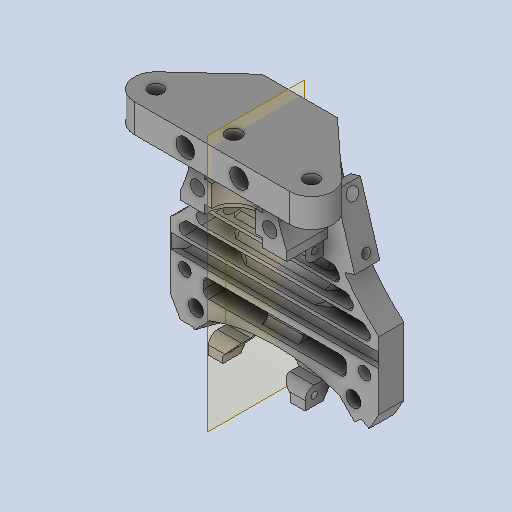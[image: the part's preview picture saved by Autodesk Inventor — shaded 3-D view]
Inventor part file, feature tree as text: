
AUTODESK INVENTOR PART (.ipt)
format: ipt  version: 2022 (Build 260153000, 153)  size: 1,126,400 bytes
history: native  units: mm
features: extrude x19, sketch x19, projected_geometry x13, reference x9, other x7, chamfer x6, fillet x4, plane x3, mirror x3, pattern_circular x1
ambient origin geometry x8: Origin, YZ Plane, XZ Plane, XY Plane, X Axis, Y Axis, Z Axis, Center Point
bodies: Solid1 (feature_tree)
feature tree (84):
  extrude  "Extrusion1"  Depth=13.0mm
  extrude  "Extrusion2"  Depth=9.0mm
  pattern_circular  "Circular Pattern1"  Count=3 Angle=360.0deg
  extrude  "Extrusion6"  Depth=7.0mm TaperAngle=0.0deg
  plane  "Work Plane1"
  extrude  "Extrusion7"  Depth=15.0mm
  extrude  "Extrusion8"  Depth=8.0mm
  extrude  "Extrusion9"  Depth=24.25mm TaperAngle=0.0deg
  fillet  "Fillet2"  Radius=30.0mm
  fillet  "Fillet3"  Radius=4.0mm
  extrude  "Extrusion10"  Depth=15.0mm
  chamfer  "Chamfer3"  Distance=3.425mm
  extrude  "Extrusion11"  TaperAngle=0.0deg  [1 undecoded]
  chamfer  "Chamfer4"  Distance=21.0mm
  extrude  "Extrusion12"  Depth=10.0mm
  extrude  "Extrusion13"  Depth=10.0mm
  extrude  "Extrusion14"  Depth=10.0mm
  extrude  "Extrusion15"  Depth=10.0mm TaperAngle=0.0deg
  extrude  "Extrusion16"  Depth=10.0mm
  mirror  "Mirror1"
  extrude  "Extrusion17"  Depth=10.0mm
  extrude  "Extrusion18"  Depth=10.0mm
  chamfer  "Chamfer5"  Distance=30.0mm
  chamfer  "Chamfer6"  Distance=30.0mm
  extrude  "Extrusion19"  Depth=10.0mm
  mirror  "Mirror2"
  plane  "Work Plane3"
  extrude  "Extrusion20"  Depth=10.0mm
  fillet  "Fillet4"  Radius=5.0mm
  mirror  "Mirror3"
  extrude  "Extrusion21"  Depth=10.0mm TaperAngle=0.0deg
  chamfer  "Chamfer7"  Distance=2.0mm
  fillet  "Fillet5"  Radius=5.0mm
  extrude  "Extrusion22"  Depth=10.0mm
  chamfer  "Chamfer8"  Distance=1.5mm
  sketch  "Sketch1"  dims[d0=25.8mm d1=13.0mm]
  sketch  "Sketch2"  dims[d2=15.0mm d3=9.0mm]
  sketch  "Sketch6"  dims[d4=8.0mm]
  sketch  "Sketch7"  dims[d5=5.0mm]
  projected_geometry  "Projected Loop1"
  projected_geometry  "Projected Loop2"
  sketch  "Sketch8"  dims[d6=25.0mm]
  sketch  "Sketch9"  dims[d7=4.0mm d8=30.0mm d10=360.0deg]
  projected_geometry  "Projected Loop3"
  projected_geometry  "Projected Loop4"
  projected_geometry  "Projected Loop5"
  projected_geometry  "Projected Loop6"
  projected_geometry  "Projected Loop7"
  sketch  "Sketch10"  dims[d12=30.0mm d14=360.0deg d16=7.0mm d17=0.0mm]
  reference  "Reference1"
  sketch  "Sketch11"  dims[d18=13.0mm d19=15.0mm]
  projected_geometry  "Projected Loop8"
  sketch  "Sketch12"  dims[d20=9.0mm d21=8.0mm]
  projected_geometry  "Projected Loop9"
  sketch  "Sketch13"  dims[d22=5.0mm d24=24.25mm d25=0.0mm d41=30.0mm d42=360.0deg d52=4.0mm]
  reference  "Reference2"
  projected_geometry  "Projected Loop10"
  sketch  "Sketch14"  dims[d53=4.0mm d54=15.0mm]
  reference  "Reference3"
  projected_geometry  "Projected Loop11"
  sketch  "Sketch15"  dims[d55=30.0mm]
  projected_geometry  "Projected Loop12"
  sketch  "Sketch16"  dims[d56=4.0mm]
  plane  "Work Plane2"
  sketch  "Sketch17"  dims[d57=4.0mm]
  sketch  "Sketch18"  dims[d58=68.718732mm]
  reference  "Reference5"
  reference  "Reference6"
  sketch  "Sketch20"  dims[d59=68.718732mm]
  reference  "Reference7"
  sketch  "Sketch21"  dims[d60=3.5mm d61=3.425mm d62=0.0mm]
  reference  "Reference8"
  reference  "Reference9"
  sketch  "Sketch22"  dims[d63=-15.0mm d64=0.0mm]
  sketch  "Sketch23"  dims[d65=11.5mm d66=21.0mm d67=2.0mm d68=2.0mm d69=12.2mm d70=6.0mm d71=0.0mm d72=8.0mm d73=4.0mm d74=40.0mm d76=5.0mm d77=10.0mm d79=10.0mm d81=30.0mm d82=30.0mm d83=2.0mm d84=2.0mm d85=5.0mm d86=3.0mm d87=0.0mm d88=2.0mm d89=5.0mm d90=0.0mm d91=1.5mm d92=1.5mm d93=9.0mm d94=9.0mm d95=4.0mm d96=4.0mm d97=43.5mm d99=0.0mm d100=0.0mm d101=12.0mm d103=12.0mm d104=8.0mm d105=0.0mm d106=4.2mm d107=6.0mm d108=2.0mm d109=45.0deg d110=0.1mm d111=0.0mm d112=5.0mm d113=2.0mm d114=45.0deg d115=11.5mm d116=0.0mm d117=2.4mm d118=0.0mm d119=4.0mm d120=0.0mm d121=0.15mm d122=0.15mm d123=4.0mm d124=4.0mm d125=4.0mm d126=4.0mm d127=10.0mm d128=0.0mm d131=7.0mm d132=0.0mm d135=18.5mm d136=3.0mm d137=2.96706mm d138=0.0mm d139=4.0mm d140=4.0mm d141=7.0mm d142=0.0mm d144=8.0mm d145=0.0mm d146=5.2mm d147=5.2mm d148=8.0mm d149=0.0mm d150=0.0mm d151=6.0mm d152=45.0deg d153=4.0mm d154=45.0deg d155=1.3mm d156=6.0mm d157=45.0deg d158=1.3mm d159=6.0mm d160=45.0deg d163=2.5mm d164=0.2mm d165=8.0mm d166=0.0mm d167=-15.615mm d168=4.0mm d169=0.0mm d170=2.0mm d171=7.5mm d172=0.0mm d173=10.0mm d174=1.8mm d175=1.8mm d176=4.0mm d177=2.0mm d178=45.0deg d179=2.0mm d180=21.75mm d181=4.2mm d182=5.0mm d183=7.0mm d188=4.2mm d189=10.0mm d190=7.0mm d191=0.0mm d192=4.0mm d193=4.0mm d194=3.0mm d195=2.0mm d196=45.0deg]
  projected_geometry  "Projected Loop13"
  reference  "Reference10"
  other  "volcano tool.iam"
  other  "E3D-VOLCANO-1.75-MO:1"
  other  "v6_Clamp V2:1"
  other  "D2HW_C202M:1"
  other  "4010 turbo fan v3:1"
  other  "toolhead v2.iam"
  other  "magnet holder V2:1"
note: 1 required parameter value undecoded (feature->parameter linkage not recoverable at this tier; creation-order binding heuristic only, values carry confidence <= 0.55)
